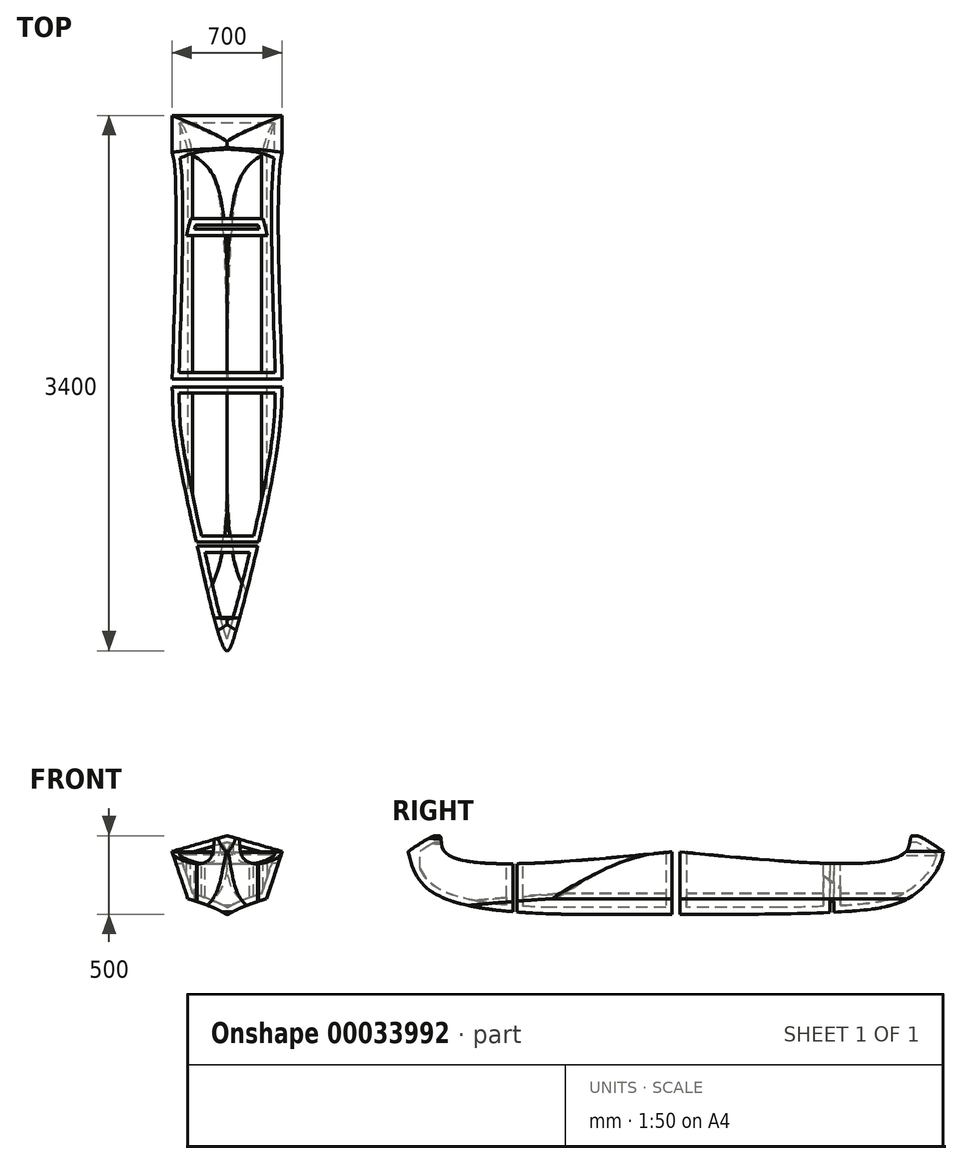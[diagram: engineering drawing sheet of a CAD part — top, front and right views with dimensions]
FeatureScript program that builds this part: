
annotation { "Feature Type Name" : "Feature", "Feature Type Description" : "" }
export const myFeature = defineFeature(function(context is Context, id is Id, definition is map)
    precondition{}
    {
        {
            var Q0;
            Q0=qCreatedBy(makeId("Front.planeOp"),FACE);
            var sketch = newSketch(context, id + "F0", { "sketchPlane" : qUnion([Q0])});
            skLineSegment(sketch, "E0.rect.bottom", {"start": v(-350, 250) * mm, "end": v(350, 250) * mm});
            skLineSegment(sketch, "E0.rect.top", {"start": v(-350, -250) * mm, "end": v(350, -250) * mm});
            skLineSegment(sketch, "E0.rect.left", {"start": v(-350, 250) * mm, "end": v(-350, -250) * mm});
            skLineSegment(sketch, "E0.rect.right", {"start": v(350, 250) * mm, "end": v(350, -250) * mm});
            skPoint(sketch, "E0.rect.middle", {"position": v(0, 0) * mm});
            skSolve(sketch);
        }
        {
            var Q0;
            Q0=makeQuery(id+"F0.imprint","IMPRINT",FACE,{"disambiguationData":[TD([[makeQuery(id+"F0.imprint","IMPRINT",EDGE,{"derivedFrom":sQuery(id+"F0.wireOp",EDGE,"E0.rect.bottom")}),-1.0]])]});
            extrude(context, id + "F1", {"entities" : qUnion([Q0]), "endBound" : BoundingType.SYMMETRIC, "depth" : 3400 * mm});
        }
        {
            var Q0;
            Q0=makeQuery(id+"F1.opExtrude","CAP_FACE",FACE,{"disambiguationData":[OSD([sQuery(id+"F0.wireOp",EDGE,"E0.rect.bottom"),sQuery(id+"F0.wireOp",EDGE,"E0.rect.top"),sQuery(id+"F0.wireOp",EDGE,"E0.rect.left"),sQuery(id+"F0.wireOp",EDGE,"E0.rect.right")])],"isStart":false});
            var sketch = newSketch(context, id + "F2", { "sketchPlane" : qUnion([Q0])});
            skLineSegment(sketch, "E1", {"start": v(-350, 150) * mm, "end": v(-250, -150) * mm});
            skLineSegment(sketch, "E2", {"start": v(350, 150) * mm, "end": v(250, -150) * mm});
            skLineSegment(sketch, "E3", {"start": v(-350, 150) * mm, "end": v(0, 250) * mm});
            skLineSegment(sketch, "E4", {"start": v(0, 250) * mm, "end": v(350, 150) * mm});
            skFitSpline(sketch, "E5", {"points": [v(-250, -150) * mm, v(0, -250) * mm, v(250, -150) * mm], "startDerivative": vector(1272.38, -379.97) * mm, "endDerivative": vector(1321.2, 405.4) * mm});
            skSolve(sketch);
        }
        {
            var Q0;
            Q0=makeQuery(id+"F1.opExtrude","SWEPT_FACE",FACE,{"disambiguationData":[OSD([sQuery(id+"F0.wireOp",EDGE,"E0.rect.right")])]});
            var sketch = newSketch(context, id + "F3", { "sketchPlane" : qUnion([Q0])});
            skPoint(sketch, "E6", {"position": v(0, 0) * mm});
            skPoint(sketch, "E7", {"position": v(-1700, 150) * mm});
            skPoint(sketch, "E8", {"position": v(1700, 150) * mm});
            skPoint(sketch, "E9", {"position": v(0, -250) * mm});
            skPoint(sketch, "E10", {"position": v(-1500, 250) * mm});
            skPoint(sketch, "E11", {"position": v(1500, 250) * mm});
            skPoint(sketch, "E12", {"position": v(0, 150) * mm});
            skFitSpline(sketch, "E13", {"points": [v(-1700, 150) * mm, v(-1500, 250) * mm, v(-1470, 150) * mm, v(0, 150) * mm], "startDerivative": vector(1122.5, 762.15) * mm, "endDerivative": vector(3396.46, 336.42) * mm});
            skFitSpline(sketch, "E14", {"points": [v(1700, 150) * mm, v(1500, 250) * mm, v(1463, 150) * mm, v(0, 150) * mm], "startDerivative": vector(-1108.51, 759.05) * mm, "endDerivative": vector(-3367.35, 333.09) * mm});
            skFitSpline(sketch, "E15", {"points": [v(-1700, 150) * mm, v(-1677.67, 66.5) * mm, v(-1586.67, -78.17) * mm, v(-1264.67, -204.17) * mm, v(-625.33, -250) * mm, v(0, -250) * mm], "startDerivative": vector(165.11, -763) * mm, "endDerivative": vector(2237.95, 18.44) * mm});
            skFitSpline(sketch, "E16", {"points": [v(1700, 150) * mm, v(1668.33, 50.17) * mm, v(1498, -134.17) * mm, v(1136.33, -227.5) * mm, v(0, -250) * mm], "startDerivative": vector(-137.44, -716.33) * mm, "endDerivative": vector(-3020.91, -0.03) * mm});
            skPoint(sketch, "E17", {"position": v(706.15, -245.82) * mm});
            skPoint(sketch, "E18", {"position": v(-877.93, -242.76) * mm});
            skSolve(sketch);
        }
        {
            var Q0;
            Q0=makeQuery(id+"F1.opExtrude","SWEPT_FACE",FACE,{"disambiguationData":[OSD([sQuery(id+"F0.wireOp",EDGE,"E0.rect.bottom")])]});
            var sketch = newSketch(context, id + "F4", { "sketchPlane" : qUnion([Q0])});
            skPoint(sketch, "E19", {"position": v(0, 1700) * mm});
            skPoint(sketch, "E20", {"position": v(0, -1700) * mm});
            skPoint(sketch, "E21", {"position": v(350, 0) * mm});
            skPoint(sketch, "E22", {"position": v(-350, 0) * mm});
            skFitSpline(sketch, "E23", {"points": [v(0, 1700) * mm, v(-49.05, 1600) * mm, v(-201.86, 1000) * mm, v(-296.68, 545.94) * mm, v(-350, 0) * mm, v(-321.15, -394.63) * mm, v(-197.7, -1000) * mm, v(-52.09, -1600) * mm, v(0, -1700) * mm, v(47.91, -1600) * mm, v(202.3, -1000) * mm, v(316.8, -423.26) * mm, v(350, 0) * mm, v(316.75, 513.18) * mm, v(198.14, 1000) * mm, v(50.95, 1600) * mm, v(0, 1700) * mm]});
            skLineSegment(sketch, "E24", {"start": v(350, 26.84) * mm, "end": v(-349.24, 26.84) * mm});
            skLineSegment(sketch, "E25", {"start": v(349.62, -23.96) * mm, "end": v(-350.43, -23.96) * mm});
            skLineSegment(sketch, "E26", {"start": v(197.17, 1003.84) * mm, "end": v(-200.95, 1003.84) * mm});
            skLineSegment(sketch, "E27", {"start": v(203.64, 978.44) * mm, "end": v(-206.97, 978.44) * mm});
            skLineSegment(sketch, "E28", {"start": v(-189.96, -1035.1) * mm, "end": v(194.08, -1035.1) * mm});
            skLineSegment(sketch, "E29", {"start": v(-195.57, -1009.7) * mm, "end": v(200.03, -1009.7) * mm});
            skSolve(sketch);
        }
        {
            var Q0;
            {var subQ1=sQuery(id+"F2.wireOp",EDGE,"E3");Q0=makeQuery(id+"F2.imprint","IMPRINT",FACE,{"disambiguationData":[TD([[makeQuery(id+"F2.imprint","IMPRINT",EDGE,{"derivedFrom":subQ1}),1.0]])]});}
            var Q1;
            {var subQ1=sQuery(id+"F2.wireOp",EDGE,"E1");Q1=makeQuery(id+"F2.imprint","IMPRINT",FACE,{"disambiguationData":[TD([[makeQuery(id+"F2.imprint","IMPRINT",EDGE,{"derivedFrom":subQ1}),-1.0]])]});}
            var Q2;
            {var subQ1=sQuery(id+"F2.wireOp",EDGE,"E2");Q2=makeQuery(id+"F2.imprint","IMPRINT",FACE,{"disambiguationData":[TD([[makeQuery(id+"F2.imprint","IMPRINT",EDGE,{"derivedFrom":subQ1}),1.0]])]});}
            var Q3;
            {var subQ1=sQuery(id+"F2.wireOp",EDGE,"E4");Q3=makeQuery(id+"F2.imprint","IMPRINT",FACE,{"disambiguationData":[TD([[makeQuery(id+"F2.imprint","IMPRINT",EDGE,{"derivedFrom":subQ1}),1.0]])]});}
            extrude(context, id + "F5", {"entities" : qUnion([Q0, Q1, Q2, Q3]), "operationType" : NewBodyOperationType.REMOVE, "endBound" : BoundingType.THROUGH_ALL, "oppositeDirection" : true, "depth" : 25.4 * mm});
        }
        {
            var Q0;
            {var subQ1=sQuery(id+"F3.wireOp",EDGE,"E14");var subQ3=sQuery(id+"F3.wireOp",EDGE,"E13");var subQ5=makeQuery(id+"F3.imprint","INTERSECT",VERTEX,{"derivedFrom":[subQ3,subQ1]});Q0=makeQuery(id+"F3.imprint","IMPRINT",FACE,{"disambiguationData":[TD([[makeQuery(id+"F3.imprint","IMPRINT",EDGE,{"disambiguationData":[TD([[subQ5,1.0]])],"derivedFrom":subQ3}),1.0]])]});}
            var Q1;
            {var subQ0=sQuery(id+"F0.wireOp",EDGE,"E0.rect.right");var subQ1=makeQuery(id+"F1.opExtrude","CAP_EDGE",EDGE,{"disambiguationData":[OSD([subQ0])],"isStart":false});var subQ2=sQuery(id+"F3.wireOp",EDGE,"E13");var subQ3=makeQuery(id+"F3.imprint","INTERSECT",VERTEX,{"derivedFrom":[subQ1,subQ2,sQuery(id+"F3.wireOp",EDGE,"E15")]});Q1=makeQuery(id+"F3.imprint","IMPRINT",FACE,{"disambiguationData":[TD([[makeQuery(id+"F3.imprint","IMPRINT",EDGE,{"disambiguationData":[TD([[subQ3,-1.0]])],"derivedFrom":subQ2}),1.0]])]});}
            var Q2;
            {var subQ0=sQuery(id+"F0.wireOp",EDGE,"E0.rect.right");var subQ1=makeQuery(id+"F1.opExtrude","CAP_EDGE",EDGE,{"disambiguationData":[OSD([subQ0])],"isStart":false});var subQ2=sQuery(id+"F3.wireOp",EDGE,"E15");var subQ3=makeQuery(id+"F3.imprint","INTERSECT",VERTEX,{"derivedFrom":[subQ1,sQuery(id+"F3.wireOp",EDGE,"E13"),subQ2]});Q2=makeQuery(id+"F3.imprint","IMPRINT",FACE,{"disambiguationData":[TD([[makeQuery(id+"F3.imprint","IMPRINT",EDGE,{"disambiguationData":[TD([[subQ3,-1.0]])],"derivedFrom":subQ2}),-1.0]])]});}
            var Q3;
            {var subQ0=sQuery(id+"F0.wireOp",EDGE,"E0.rect.right");var subQ1=makeQuery(id+"F1.opExtrude","CAP_EDGE",EDGE,{"disambiguationData":[OSD([subQ0])],"isStart":true});var subQ2=sQuery(id+"F3.wireOp",EDGE,"E14");var subQ3=makeQuery(id+"F3.imprint","INTERSECT",VERTEX,{"derivedFrom":[subQ1,subQ2,sQuery(id+"F3.wireOp",EDGE,"E16")]});Q3=makeQuery(id+"F3.imprint","IMPRINT",FACE,{"disambiguationData":[TD([[makeQuery(id+"F3.imprint","IMPRINT",EDGE,{"disambiguationData":[TD([[subQ3,-1.0]])],"derivedFrom":subQ2}),-1.0]])]});}
            var Q4;
            {var subQ2=sQuery(id+"F3.wireOp",EDGE,"E16");Q4=makeQuery(id+"F3.imprint","IMPRINT",FACE,{"disambiguationData":[TD([[makeQuery(id+"F3.imprint","IMPRINT",EDGE,{"derivedFrom":subQ2}),1.0]])]});}
            extrude(context, id + "F6", {"entities" : qUnion([Q0, Q1, Q2, Q3, Q4]), "operationType" : NewBodyOperationType.REMOVE, "endBound" : BoundingType.THROUGH_ALL, "oppositeDirection" : true, "depth" : 25.4 * mm});
        }
        {
            var Q0;
            {var subQ0=sQuery(id+"F0.wireOp",EDGE,"E0.rect.bottom");var subQ1=makeQuery(id+"F1.opExtrude","CAP_EDGE",EDGE,{"disambiguationData":[OSD([subQ0])],"isStart":true});var subQ2=sQuery(id+"F4.wireOp",EDGE,"E23");var subQ3=makeQuery(id+"F4.imprint","INTERSECT",VERTEX,{"disambiguationData":[OD(0.0)],"derivedFrom":[subQ1,subQ2]});Q0=makeQuery(id+"F4.imprint","IMPRINT",FACE,{"disambiguationData":[TD([[makeQuery(id+"F4.imprint","IMPRINT",EDGE,{"disambiguationData":[TD([[subQ3,-1.0]])],"derivedFrom":subQ2}),-1.0]])]});}
            var Q1;
            {var subQ0=sQuery(id+"F0.wireOp",EDGE,"E0.rect.bottom");var subQ1=makeQuery(id+"F1.opExtrude","CAP_EDGE",EDGE,{"disambiguationData":[OSD([subQ0])],"isStart":true});var subQ2=sQuery(id+"F4.wireOp",EDGE,"E23");var subQ3=makeQuery(id+"F4.imprint","INTERSECT",VERTEX,{"disambiguationData":[OD(1.0)],"derivedFrom":[subQ1,subQ2]});Q1=makeQuery(id+"F4.imprint","IMPRINT",FACE,{"disambiguationData":[TD([[makeQuery(id+"F4.imprint","IMPRINT",EDGE,{"disambiguationData":[TD([[subQ3,1.0]])],"derivedFrom":subQ2}),-1.0]])]});}
            var Q2;
            {var subQ0=sQuery(id+"F0.wireOp",EDGE,"E0.rect.bottom");var subQ1=makeQuery(id+"F1.opExtrude","CAP_EDGE",EDGE,{"disambiguationData":[OSD([subQ0])],"isStart":false});var subQ2=sQuery(id+"F4.wireOp",EDGE,"E23");var subQ3=makeQuery(id+"F4.imprint","INTERSECT",VERTEX,{"disambiguationData":[OD(0.0)],"derivedFrom":[subQ1,subQ2]});Q2=makeQuery(id+"F4.imprint","IMPRINT",FACE,{"disambiguationData":[TD([[makeQuery(id+"F4.imprint","IMPRINT",EDGE,{"disambiguationData":[TD([[subQ3,1.0]])],"derivedFrom":subQ2}),-1.0]])]});}
            var Q3;
            {var subQ0=sQuery(id+"F0.wireOp",EDGE,"E0.rect.bottom");var subQ1=makeQuery(id+"F1.opExtrude","CAP_EDGE",EDGE,{"disambiguationData":[OSD([subQ0])],"isStart":false});var subQ2=sQuery(id+"F4.wireOp",EDGE,"E23");var subQ3=makeQuery(id+"F4.imprint","INTERSECT",VERTEX,{"disambiguationData":[OD(1.0)],"derivedFrom":[subQ1,subQ2]});Q3=makeQuery(id+"F4.imprint","IMPRINT",FACE,{"disambiguationData":[TD([[makeQuery(id+"F4.imprint","IMPRINT",EDGE,{"disambiguationData":[TD([[subQ3,-1.0]])],"derivedFrom":subQ2}),-1.0]])]});}
            extrude(context, id + "F7", {"entities" : qUnion([Q0, Q1, Q2, Q3]), "operationType" : NewBodyOperationType.REMOVE, "endBound" : BoundingType.THROUGH_ALL, "oppositeDirection" : true, "depth" : 25.4 * mm});
        }
        {
            var Q0;
            {var subQ1=sQuery(id+"F4.wireOp",EDGE,"E26");Q0=makeQuery(id+"F4.imprint","IMPRINT",FACE,{"disambiguationData":[TD([[makeQuery(id+"F4.imprint","IMPRINT",EDGE,{"derivedFrom":subQ1}),1.0]])]});}
            var Q1;
            {var subQ4=sQuery(id+"F4.wireOp",EDGE,"E24");Q1=makeQuery(id+"F4.imprint","IMPRINT",FACE,{"disambiguationData":[TD([[makeQuery(id+"F4.imprint","IMPRINT",EDGE,{"derivedFrom":subQ4}),1.0]])]});}
            var Q2;
            {var subQ1=sQuery(id+"F4.wireOp",EDGE,"E28");Q2=makeQuery(id+"F4.imprint","IMPRINT",FACE,{"disambiguationData":[TD([[makeQuery(id+"F4.imprint","IMPRINT",EDGE,{"derivedFrom":subQ1}),1.0]])]});}
            var Q3;
            {var subQ0=sQuery(id+"F4.wireOp",EDGE,"3a1ef058-1c18-4de9-ba3c-28d1524b7c65");Q3=makeQuery(id+"F4.imprint","IMPRINT",FACE,{"disambiguationData":[TD([[makeQuery(id+"F4.imprint","IMPRINT",EDGE,{"derivedFrom":subQ0}),-1.0]])]});}
            extrude(context, id + "F8", {"entities" : qUnion([Q0, Q1, Q2, Q3]), "operationType" : NewBodyOperationType.REMOVE, "endBound" : BoundingType.THROUGH_ALL, "oppositeDirection" : true, "depth" : 25.4 * mm});
        }
        {
            var Q0;
            {var subQ0=sQuery(id+"F3.wireOp",EDGE,"E14");var subQ3=sQuery(id+"F4.wireOp",EDGE,"E24");Q0=makeQuery(id+"F8.boolean.opBoolean","SPLIT",FACE,{"disambiguationData":[TD([makeQuery(id+"F8.opExtrude","SWEPT_FACE",FACE,{"disambiguationData":[OSD([subQ3])]})])],"derivedFrom":makeQuery(id+"F6.boolean.opBoolean","COPY",FACE,{"derivedFrom":makeQuery(id+"F6.opExtrude","SWEPT_FACE",FACE,{"disambiguationData":[OSD([subQ0]),TDD([makeQuery(id+"F3.imprint","IMPRINT",EDGE,{"disambiguationData":[TD([[makeQuery(id+"F3.imprint","INTERSECT",VERTEX,{"derivedFrom":[sQuery(id+"F3.wireOp",EDGE,"E13"),subQ0]}),1.0]])],"derivedFrom":subQ0})])]})})});}
            var Q1;
            {var subQ0=sQuery(id+"F3.wireOp",EDGE,"E13");var subQ3=sQuery(id+"F3.wireOp",EDGE,"E14");var subQ4=makeQuery(id+"F3.imprint","INTERSECT",VERTEX,{"derivedFrom":[subQ0,subQ3]});Q1=makeQuery(id+"F8.boolean.opBoolean","SPLIT",FACE,{"disambiguationData":[TD([makeQuery(id+"F5.boolean.opBoolean","COPY",FACE,{"derivedFrom":makeQuery(id+"F5.opExtrude","SWEPT_FACE",FACE,{"disambiguationData":[OSD([sQuery(id+"F2.wireOp",EDGE,"E1")])]})})])],"derivedFrom":makeQuery(id+"F6.boolean.opBoolean","COPY",FACE,{"derivedFrom":makeQuery(id+"F6.opExtrude","SWEPT_FACE",FACE,{"disambiguationData":[OSD([subQ0]),TDD([makeQuery(id+"F3.imprint","IMPRINT",EDGE,{"disambiguationData":[TD([[subQ4,1.0]])],"derivedFrom":subQ0})])]})})});}
            var Q2;
            {var subQ0=sQuery(id+"F3.wireOp",EDGE,"E13");Q2=makeQuery(id+"F8.boolean.opBoolean","SPLIT",FACE,{"disambiguationData":[TD([makeQuery(id+"F5.boolean.opBoolean","COPY",FACE,{"derivedFrom":makeQuery(id+"F5.opExtrude","SWEPT_FACE",FACE,{"disambiguationData":[OSD([sQuery(id+"F2.wireOp",EDGE,"E3")])]})})])],"derivedFrom":makeQuery(id+"F6.boolean.opBoolean","COPY",FACE,{"derivedFrom":makeQuery(id+"F6.opExtrude","SWEPT_FACE",FACE,{"disambiguationData":[OSD([subQ0]),TDD([makeQuery(id+"F3.imprint","IMPRINT",EDGE,{"disambiguationData":[TD([[makeQuery(id+"F3.imprint","INTERSECT",VERTEX,{"derivedFrom":[subQ0,sQuery(id+"F3.wireOp",EDGE,"E14")]}),1.0]])],"derivedFrom":subQ0})])]})})});}
            var Q3;
            {var subQ0=sQuery(id+"F3.wireOp",EDGE,"E14");Q3=makeQuery(id+"F8.boolean.opBoolean","SPLIT",FACE,{"disambiguationData":[TD([makeQuery(id+"F5.boolean.opBoolean","COPY",FACE,{"derivedFrom":makeQuery(id+"F5.opExtrude","SWEPT_FACE",FACE,{"disambiguationData":[OSD([sQuery(id+"F2.wireOp",EDGE,"E3")])]})})])],"derivedFrom":makeQuery(id+"F6.boolean.opBoolean","COPY",FACE,{"derivedFrom":makeQuery(id+"F6.opExtrude","SWEPT_FACE",FACE,{"disambiguationData":[OSD([subQ0]),TDD([makeQuery(id+"F3.imprint","IMPRINT",EDGE,{"disambiguationData":[TD([[makeQuery(id+"F3.imprint","INTERSECT",VERTEX,{"derivedFrom":[sQuery(id+"F3.wireOp",EDGE,"E13"),subQ0]}),1.0]])],"derivedFrom":subQ0})])]})})});}
            shell(context, id + "F9", {"entities" : qUnion([Q0, Q1, Q2, Q3]), "thickness" : 40 * mm});
        }
    });
